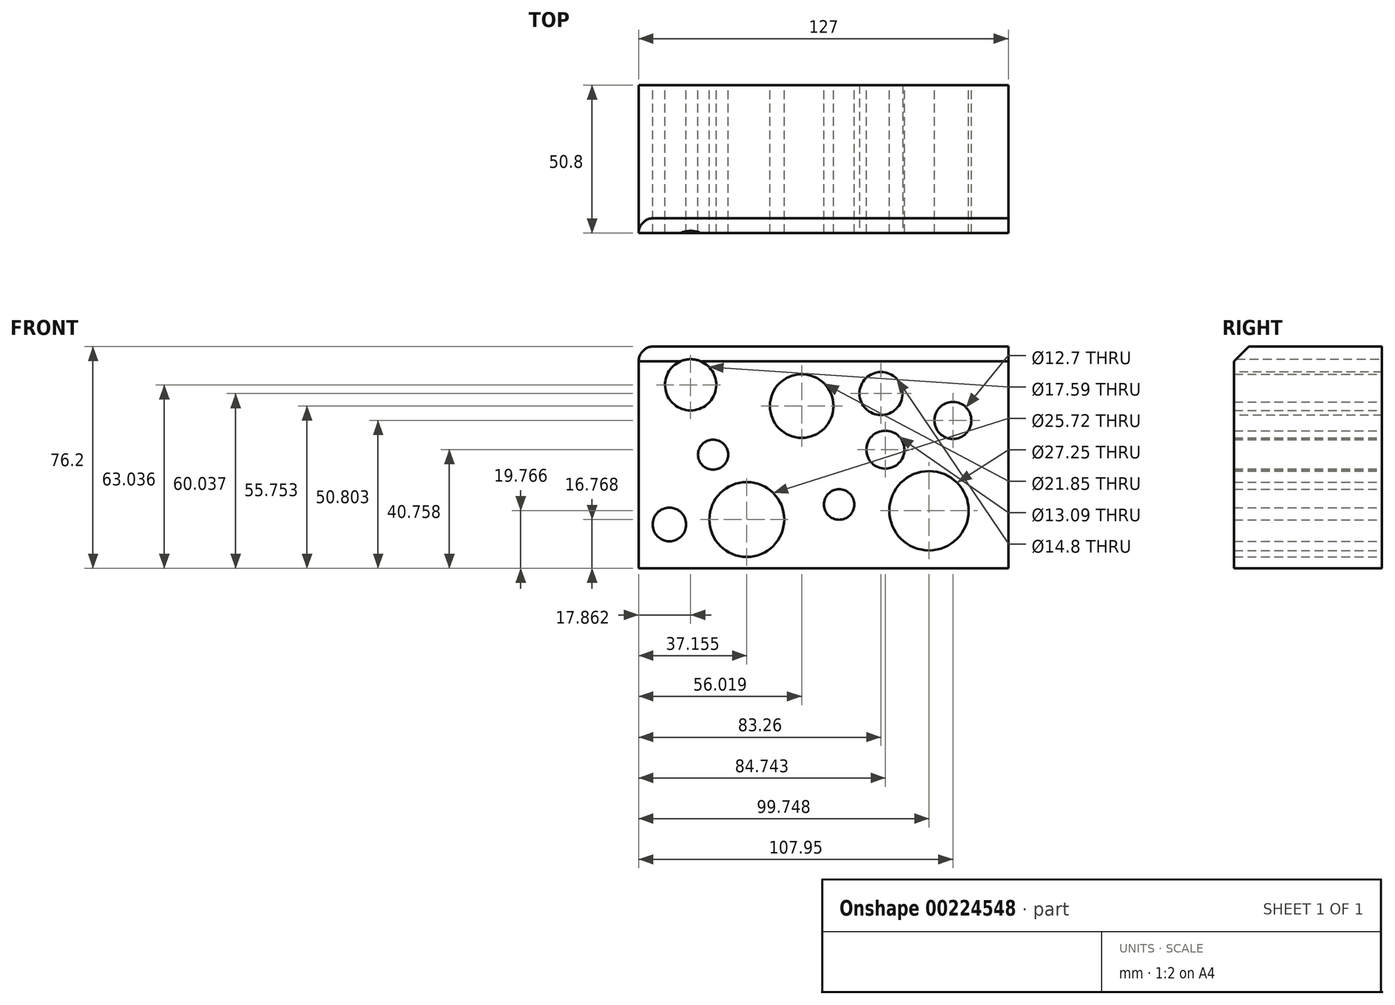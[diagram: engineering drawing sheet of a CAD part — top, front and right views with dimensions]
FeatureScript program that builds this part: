
annotation { "Feature Type Name" : "Feature", "Feature Type Description" : "" }
export const myFeature = defineFeature(function(context is Context, id is Id, definition is map)
    precondition{}
    {
        {
            var Q0;
            Q0=qCreatedBy(makeId("Front.planeOp"),FACE);
            var sketch = newSketch(context, id + "F0", { "sketchPlane" : qUnion([Q0])});
            skLineSegment(sketch, "E0.bottom", {"start": v(-61.5, 41.82) * mm, "end": v(65.5, 41.82) * mm});
            skLineSegment(sketch, "E0.top", {"start": v(-61.5, -34.38) * mm, "end": v(65.5, -34.38) * mm});
            skLineSegment(sketch, "E0.left", {"start": v(-61.5, 41.82) * mm, "end": v(-61.5, -34.38) * mm});
            skLineSegment(sketch, "E0.right", {"start": v(65.5, 41.82) * mm, "end": v(65.5, -34.38) * mm});
            skCircle(sketch, "E1", {"center": v(46.45, 16.42) * mm, "radius": 6.35 * mm});
            skCircle(sketch, "E2", {"center": v(-43.64, 28.66) * mm, "radius": 8.8 * mm});
            skCircle(sketch, "E3", {"center": v(-24.35, -17.61) * mm, "radius": 12.86 * mm});
            skCircle(sketch, "E4", {"center": v(38.25, -14.61) * mm, "radius": 13.62 * mm});
            skCircle(sketch, "E5", {"center": v(-5.48, 21.37) * mm, "radius": 10.93 * mm});
            skCircle(sketch, "E6", {"center": v(-35.92, 4.66) * mm, "radius": 5.18 * mm});
            skCircle(sketch, "E7", {"center": v(23.24, 6.38) * mm, "radius": 6.54 * mm});
            skCircle(sketch, "E8", {"center": v(7.38, -12.47) * mm, "radius": 5.23 * mm});
            skCircle(sketch, "E9", {"center": v(-50.93, -19.33) * mm, "radius": 5.77 * mm});
            skSolve(sketch);
        }
        {
            var Q0;
            Q0=makeQuery(id+"F0.imprint","IMPRINT",FACE,{"disambiguationData":[TD([[makeQuery(id+"F0.imprint","IMPRINT",EDGE,{"derivedFrom":sQuery(id+"F0.wireOp",EDGE,"E0.bottom")}),-1.0]])]});
            extrude(context, id + "F1", {"entities" : qUnion([Q0]), "depth" : 50.8 * mm});
        }
        {
            var Q0;
            Q0=makeQuery(id+"F1.opExtrude","CAP_FACE",FACE,{"disambiguationData":[OSD([sQuery(id+"F0.wireOp",EDGE,"E0.bottom"),sQuery(id+"F0.wireOp",EDGE,"E0.top"),sQuery(id+"F0.wireOp",EDGE,"E0.left"),sQuery(id+"F0.wireOp",EDGE,"E0.right"),sQuery(id+"F0.wireOp",EDGE,"E1"),sQuery(id+"F0.wireOp",EDGE,"E2"),sQuery(id+"F0.wireOp",EDGE,"E3"),sQuery(id+"F0.wireOp",EDGE,"E4"),sQuery(id+"F0.wireOp",EDGE,"E5"),sQuery(id+"F0.wireOp",EDGE,"E6"),sQuery(id+"F0.wireOp",EDGE,"E7"),sQuery(id+"F0.wireOp",EDGE,"E8"),sQuery(id+"F0.wireOp",EDGE,"E9")])],"isStart":false});
            var sketch = newSketch(context, id + "F2", { "sketchPlane" : qUnion([Q0])});
            skCircle(sketch, "E10", {"center": v(21.76, 25.66) * mm, "radius": 7.4 * mm});
            skSolve(sketch);
        }
        {
            var Q0;
            Q0=makeQuery(id+"F2.imprint","IMPRINT",FACE,{"disambiguationData":[TD([[makeQuery(id+"F2.imprint","IMPRINT",EDGE,{"derivedFrom":sQuery(id+"F2.wireOp",EDGE,"E10")}),1.0]])]});
            extrude(context, id + "F3", {"entities" : qUnion([Q0]), "operationType" : NewBodyOperationType.REMOVE, "oppositeDirection" : true, "depth" : 51.05 * mm});
        }
        {
            var Q0;
            Q0=makeQuery(id+"F1.opExtrude","CAP_EDGE",EDGE,{"disambiguationData":[OSD([sQuery(id+"F0.wireOp",EDGE,"E0.bottom")])],"isStart":false});
            chamfer(context, id + "F4", {"entities" : qUnion([Q0]), "width" : 5.08 * mm, "tangentPropagation" : true});
        }
        {
            var Q0;
            Q0=makeQuery(id+"F1.opExtrude","SWEPT_EDGE",EDGE,{"disambiguationData":[OSD([sQuery(id+"F0.wireOp",EDGE,"E0.bottom"),sQuery(id+"F0.wireOp",EDGE,"E0.left")])]});
            fillet(context, id + "F5", {"entities" : qUnion([Q0]), "radius" : 5.08 * mm, "tangentPropagation" : true, "allowEdgeOverflow" : false});
        }
    });
